# Revit family: Electrical_Distribution_ABB_MTR-STACK-2-125A-RING-SKT-10-22K
name_source: partatom
category: Electrical Equipment
units: mm (PartAtom-declared; Revit-internal decimal feet)

## family parameters
Cut with Voids When Loaded = No
Host = Face
OmniClass Number = 23.35.31.27
Panel Configuration = Two Columns, Circuits Across
Part Type = Panelboard
Room Calculation Point = No
Round Connector Dimension = Use Diameter
Shared = No

## types (4) — shared parameters
Apparent Load = 0 VA
Bypass = None
Cover material = ABB - Plastic - Grey
Date Updated = 2023/09/01
Default Elevation = 4' - 0"
Enclosure = N3R Outdoor
Factory Installed Jaw Configuration = 4-Jaw
Manufacturer = ABB
Number of Sockets = 2
Primary material = ABB - Steel - White
Product data url = https://www.bimobject.com
Socket Amps = 125 A
Socket Phase Output = Single Phase
Socket Type = Ring
Tenant Breakers = Only Accepts 10-22 KAIC THQL/THHQL Tenant Breakers
URL = https://new.abb.com
Version = 1
Voltage = 120/240V
Voltage (V) = 120 V
zero-valued in all types: Power Factor

## per-type parameters (varying)
| type | Description | Horizontal Bus Amperage | Main Phase Input | Number of Poles |
| RMS28212LRGR | MTR STACK 2-125A 3PH-1PH RING SKT 10-22K | 800 A | Three Phase | 3 |
| RMS18212LRGR | MTR STACK 2-125A 1PH-1PH RING SKT 10-22K | 800 A | Single Phase | 2 |
| RMS212212LRGR | MTR STACK 2-125A 3PH-1PH RING SKT 10-22K | 1200 A | Three Phase | 3 |
| RMS112212LRGR | MTR STACK 2-125A 1PH-1PH RING SKT 10-22K | 1200 A | Single Phase | 2 |

note: column(s) folded — value = type name in every type: Model

## geometry (parser evidence)
native form markers: Sweep x14
no freeform markers — native parametric forms only
